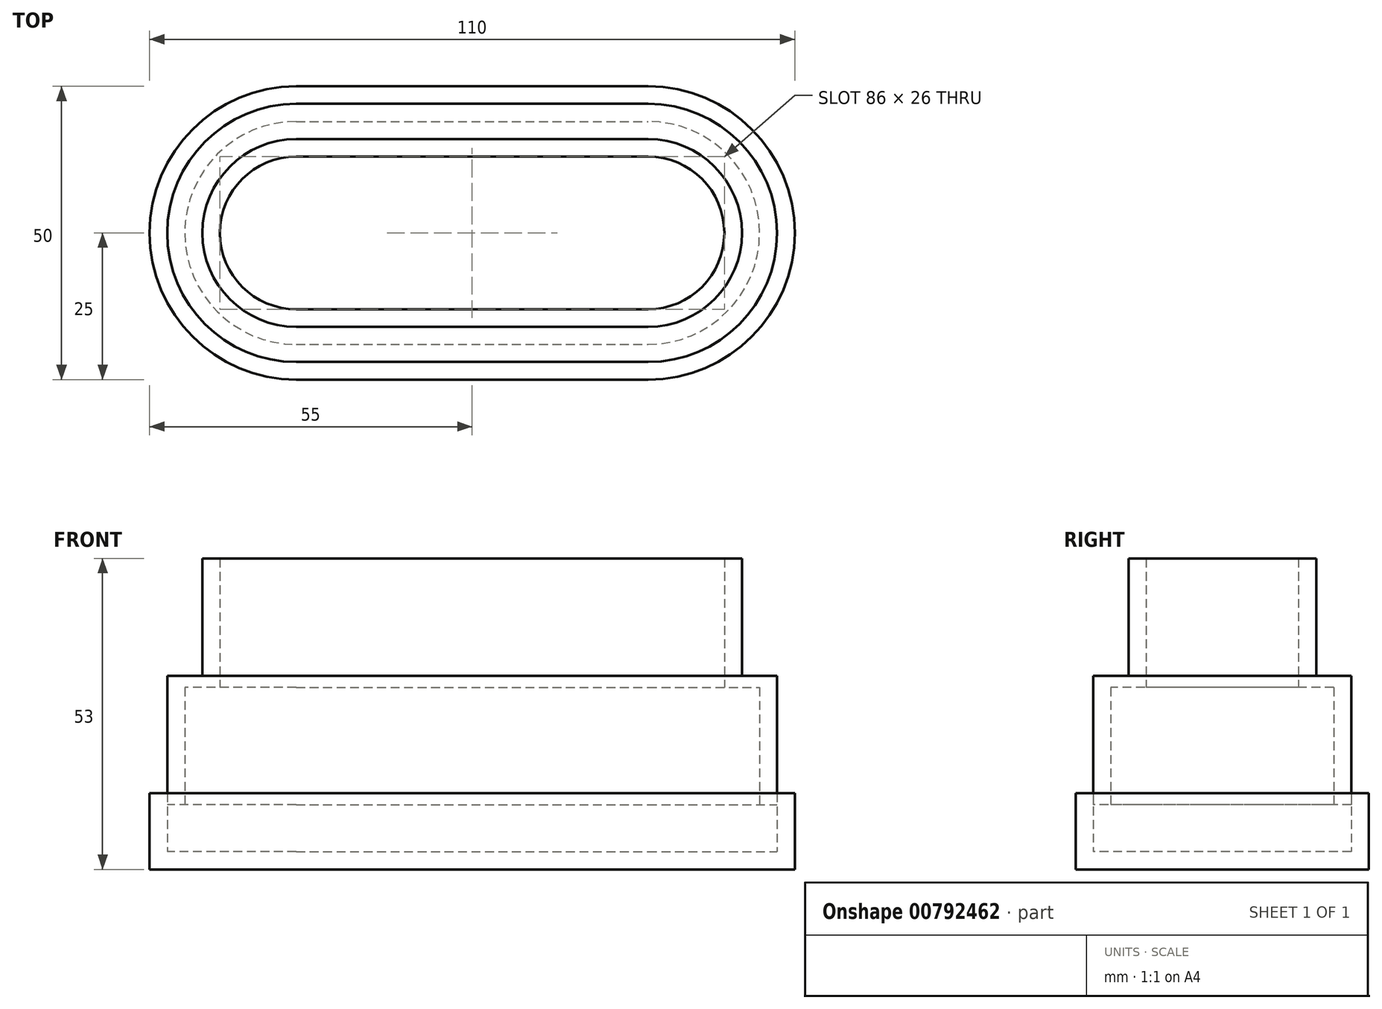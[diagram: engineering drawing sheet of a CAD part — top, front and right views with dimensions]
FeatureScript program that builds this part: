
annotation { "Feature Type Name" : "Feature", "Feature Type Description" : "" }
export const myFeature = defineFeature(function(context is Context, id is Id, definition is map)
    precondition{}
    {
        {
            var Q0;
            Q0=qCreatedBy(makeId("Top.planeOp"),FACE);
            var sketch = newSketch(context, id + "F0", { "sketchPlane" : qUnion([Q0])});
            skArc(sketch, "E0", {"start": v(-30, 25) * mm, "mid": v(-55, 0) * mm, "end": v(-30, -25) * mm});
            skArc(sketch, "E1", {"start": v(30, -25) * mm, "mid": v(55, 0) * mm, "end": v(30, 25) * mm});
            skLineSegment(sketch, "E2.bottom", {"start": v(-30, 25) * mm, "end": v(30, 25) * mm});
            skLineSegment(sketch, "E2.top", {"start": v(-30, -25) * mm, "end": v(30, -25) * mm});
            skArc(sketch, "E3.0", {"start": v(-30, 22) * mm, "mid": v(-52, 0) * mm, "end": v(-30, -22) * mm});
            skLineSegment(sketch, "E3.1", {"start": v(-30, 22) * mm, "end": v(30, 22) * mm});
            skArc(sketch, "E3.2", {"start": v(30, -22) * mm, "mid": v(52, 0) * mm, "end": v(30, 22) * mm});
            skLineSegment(sketch, "E3.3", {"start": v(-30, -22) * mm, "end": v(30, -22) * mm});
            skSolve(sketch);
        }
        {
            var Q0;
            Q0=makeQuery(id+"F0.imprint","IMPRINT",FACE,{"disambiguationData":[TD([[makeQuery(id+"F0.imprint","IMPRINT",EDGE,{"derivedFrom":sQuery(id+"F0.wireOp",EDGE,"E3.0")}),1.0]])]});
            var Q1;
            Q1=makeQuery(id+"F0.imprint","IMPRINT",FACE,{"disambiguationData":[TD([[makeQuery(id+"F0.imprint","IMPRINT",EDGE,{"derivedFrom":sQuery(id+"F0.wireOp",EDGE,"E0")}),1.0]])]});
            extrude(context, id + "F1", {"entities" : qUnion([Q0, Q1]), "oppositeDirection" : true, "depth" : 3 * mm, "offsetDistance" : 25 * mm});
        }
        {
            var Q0;
            Q0=makeQuery(id+"F0.imprint","IMPRINT",FACE,{"disambiguationData":[TD([[makeQuery(id+"F0.imprint","IMPRINT",EDGE,{"derivedFrom":sQuery(id+"F0.wireOp",EDGE,"E0")}),1.0]])]});
            extrude(context, id + "F2", {"entities" : qUnion([Q0]), "operationType" : NewBodyOperationType.ADD, "depth" : 10 * mm, "offsetDistance" : 25 * mm});
        }
        {
            var Q0;
            Q0=makeQuery(id+"F2.opExtrude","CAP_FACE",FACE,{"disambiguationData":[OSD([sQuery(id+"F0.wireOp",EDGE,"E0"),sQuery(id+"F0.wireOp",EDGE,"E1"),sQuery(id+"F0.wireOp",EDGE,"E2.bottom"),sQuery(id+"F0.wireOp",EDGE,"E2.top"),sQuery(id+"F0.wireOp",EDGE,"E3.0"),sQuery(id+"F0.wireOp",EDGE,"E3.1"),sQuery(id+"F0.wireOp",EDGE,"E3.2"),sQuery(id+"F0.wireOp",EDGE,"E3.3")])],"isStart":false});
            var sketch = newSketch(context, id + "F3", { "sketchPlane" : qUnion([Q0])});
            skArc(sketch, "E4.0", {"start": v(-30, 22) * mm, "mid": v(-52, 0) * mm, "end": v(-30, -22) * mm});
            skLineSegment(sketch, "E4.1", {"start": v(-30, 22) * mm, "end": v(30, 22) * mm});
            skArc(sketch, "E4.2", {"start": v(30, -22) * mm, "mid": v(52, 0) * mm, "end": v(30, 22) * mm});
            skLineSegment(sketch, "E4.3", {"start": v(-30, -22) * mm, "end": v(30, -22) * mm});
            skArc(sketch, "E5.0", {"start": v(-30, 19) * mm, "mid": v(-49, 0) * mm, "end": v(-30, -19) * mm});
            skLineSegment(sketch, "E5.1", {"start": v(-30, 19) * mm, "end": v(30, 19) * mm});
            skArc(sketch, "E5.2", {"start": v(30, -19) * mm, "mid": v(49, 0) * mm, "end": v(30, 19) * mm});
            skLineSegment(sketch, "E5.3", {"start": v(-30, -19) * mm, "end": v(30, -19) * mm});
            skSolve(sketch);
        }
        {
            var Q0;
            Q0=makeQuery(id+"F3.imprint","IMPRINT",FACE,{"disambiguationData":[TD([[makeQuery(id+"F3.imprint","IMPRINT",EDGE,{"derivedFrom":sQuery(id+"F3.wireOp",EDGE,"E4.0")}),1.0]])]});
            extrude(context, id + "F4", {"entities" : qUnion([Q0]), "depth" : 20 * mm, "offsetDistance" : 25 * mm, "hasSecondDirection" : true, "secondDirectionOppositeDirection" : true, "secondDirectionDepth" : 2 * mm});
        }
        {
            var Q0;
            Q0=makeQuery(id+"F4.opExtrude","CAP_FACE",FACE,{"disambiguationData":[OSD([sQuery(id+"F3.wireOp",EDGE,"E4.0"),sQuery(id+"F3.wireOp",EDGE,"E4.1"),sQuery(id+"F3.wireOp",EDGE,"E4.2"),sQuery(id+"F3.wireOp",EDGE,"E4.3"),sQuery(id+"F3.wireOp",EDGE,"E5.0"),sQuery(id+"F3.wireOp",EDGE,"E5.1"),sQuery(id+"F3.wireOp",EDGE,"E5.2"),sQuery(id+"F3.wireOp",EDGE,"E5.3")])],"isStart":false});
            var sketch = newSketch(context, id + "F5", { "sketchPlane" : qUnion([Q0])});
            skArc(sketch, "E6.0", {"start": v(-30, 19) * mm, "mid": v(-49, 0) * mm, "end": v(-30, -19) * mm});
            skLineSegment(sketch, "E6.1", {"start": v(-30, 19) * mm, "end": v(30, 19) * mm});
            skArc(sketch, "E6.2", {"start": v(30, -19) * mm, "mid": v(49, 0) * mm, "end": v(30, 19) * mm});
            skLineSegment(sketch, "E6.3", {"start": v(-30, -19) * mm, "end": v(30, -19) * mm});
            skLineSegment(sketch, "E7.0", {"start": v(-30, 16) * mm, "end": v(30, 16) * mm});
            skArc(sketch, "E7.1", {"start": v(-30, 16) * mm, "mid": v(-46, 0) * mm, "end": v(-30, -16) * mm});
            skLineSegment(sketch, "E7.2", {"start": v(-30, -16) * mm, "end": v(30, -16) * mm});
            skArc(sketch, "E7.3", {"start": v(30, -16) * mm, "mid": v(46, 0) * mm, "end": v(30, 16) * mm});
            skArc(sketch, "E8.0", {"start": v(-30, 13) * mm, "mid": v(-43, 0) * mm, "end": v(-30, -13) * mm});
            skLineSegment(sketch, "E8.1", {"start": v(-30, 13) * mm, "end": v(30, 13) * mm});
            skArc(sketch, "E8.2", {"start": v(30, -13) * mm, "mid": v(43, 0) * mm, "end": v(30, 13) * mm});
            skLineSegment(sketch, "E8.3", {"start": v(-30, -13) * mm, "end": v(30, -13) * mm});
            skSolve(sketch);
        }
        {
            var Q0;
            Q0=makeQuery(id+"F5.imprint","IMPRINT",FACE,{"disambiguationData":[TD([[makeQuery(id+"F5.imprint","IMPRINT",EDGE,{"derivedFrom":sQuery(id+"F5.wireOp",EDGE,"E7.0")}),-1.0]])]});
            extrude(context, id + "F6", {"entities" : qUnion([Q0]), "depth" : 20 * mm, "offsetDistance" : 25 * mm, "hasSecondDirection" : true, "secondDirectionOppositeDirection" : true, "secondDirectionDepth" : 2 * mm});
        }
        {
            var Q0;
            Q0=makeQuery(id+"F5.imprint","IMPRINT",FACE,{"disambiguationData":[TD([[makeQuery(id+"F5.imprint","IMPRINT",EDGE,{"derivedFrom":sQuery(id+"F5.wireOp",EDGE,"E6.0")}),1.0]])]});
            extrude(context, id + "F7", {"entities" : qUnion([Q0]), "operationType" : NewBodyOperationType.ADD, "oppositeDirection" : true, "depth" : 2 * mm, "offsetDistance" : 25 * mm});
        }
    });
